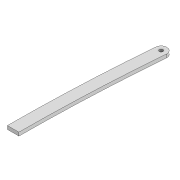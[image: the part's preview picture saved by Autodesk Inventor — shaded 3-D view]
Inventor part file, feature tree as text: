
AUTODESK INVENTOR PART (.ipt)
format: ipt  version: 2022 (Build 260153000, 153)  size: 101,888 bytes
history: native  units: mm
features: extrude x2, sketch x2
ambient origin geometry x8: Origin, YZ Plane, XZ Plane, XY Plane, X Axis, Y Axis, Z Axis, Center Point
bodies: Solid1 (feature_tree)
feature tree (4):
  extrude  "Extrusion1"  Depth=3.3mm
  extrude  "Extrusion2"  Depth=253.429mm
  sketch  "Sketch1"  dims[d0=3.3mm d1=3.3mm]
  sketch  "Sketch2"  dims[d2=10.0mm d3=253.429mm d6=3.0mm d7=0.0mm d16=1500.0mm d17=1500.0mm d18=10.0mm d19=0.0mm]
